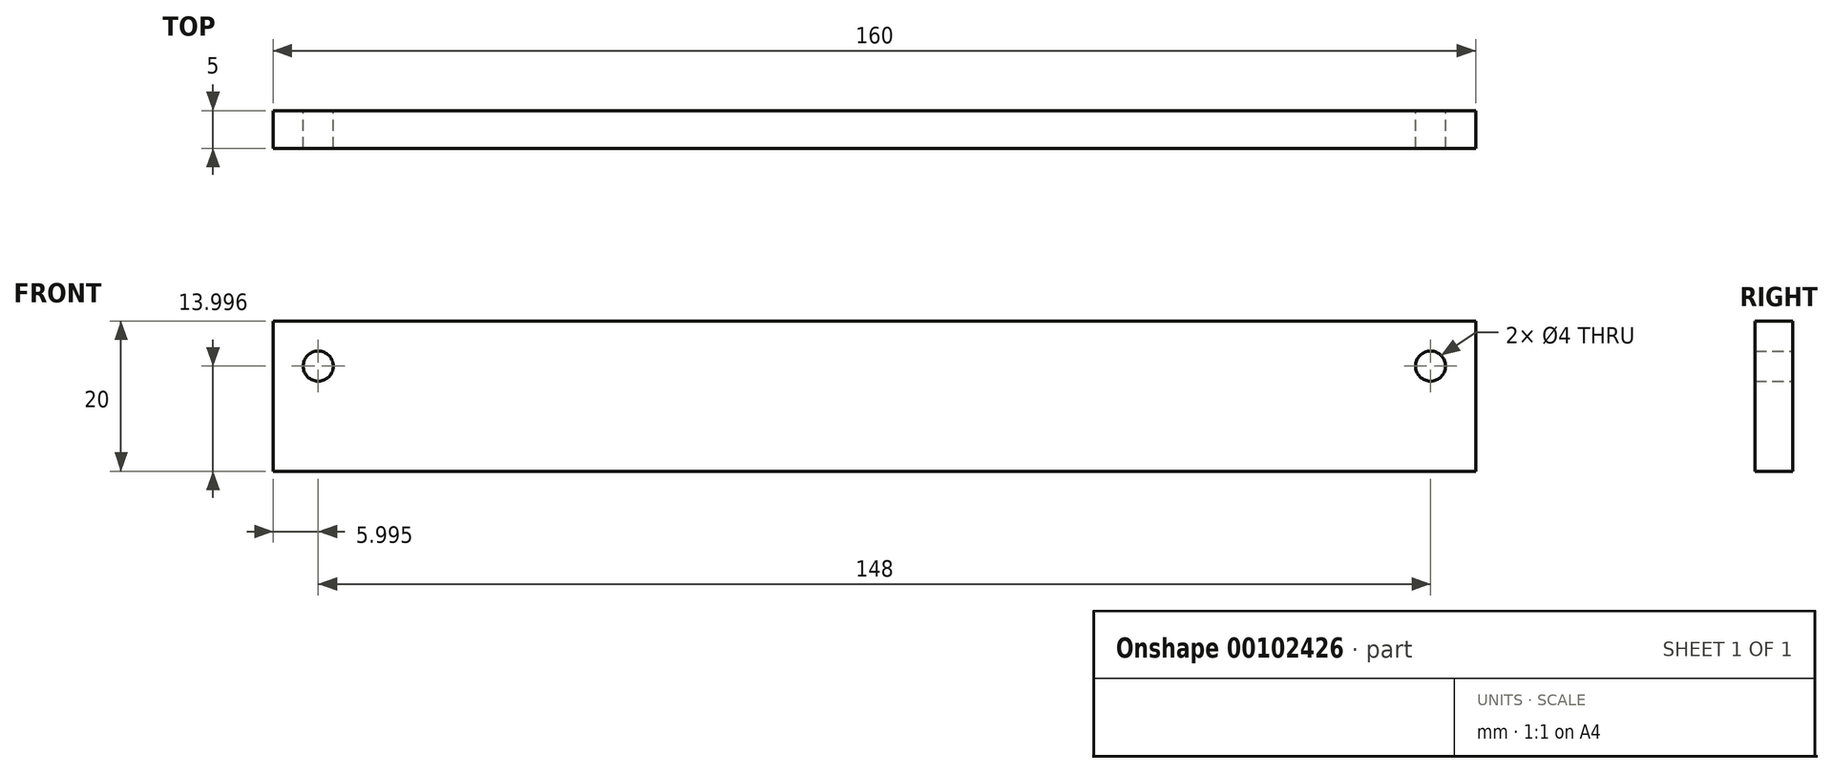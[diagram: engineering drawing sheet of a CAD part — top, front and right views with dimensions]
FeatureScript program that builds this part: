
annotation { "Feature Type Name" : "Feature", "Feature Type Description" : "" }
export const myFeature = defineFeature(function(context is Context, id is Id, definition is map)
    precondition{}
    {
        {
            var Q0;
            Q0=qCreatedBy(makeId("Front.planeOp"),FACE);
            var sketch = newSketch(context, id + "F0", { "sketchPlane" : qUnion([Q0])});
            skLineSegment(sketch, "E0.bottom", {"start": v(-39.16, 10.86) * mm, "end": v(120.84, 10.86) * mm});
            skLineSegment(sketch, "E0.top", {"start": v(-39.16, -9.14) * mm, "end": v(120.84, -9.14) * mm});
            skLineSegment(sketch, "E0.left", {"start": v(-39.16, 10.86) * mm, "end": v(-39.16, -9.14) * mm});
            skLineSegment(sketch, "E0.right", {"start": v(120.84, 10.86) * mm, "end": v(120.84, -9.14) * mm});
            skCircle(sketch, "E1", {"center": v(-33.16, 4.86) * mm, "radius": 2 * mm});
            skCircle(sketch, "E2", {"center": v(114.84, 4.86) * mm, "radius": 2 * mm});
            skSolve(sketch);
        }
        {
            var Q0;
            Q0=makeQuery(id+"F0.imprint","IMPRINT",FACE,{"disambiguationData":[TD([[makeQuery(id+"F0.imprint","IMPRINT",EDGE,{"derivedFrom":sQuery(id+"F0.wireOp",EDGE,"E0.bottom")}),-1.0]])]});
            extrude(context, id + "F1", {"entities" : qUnion([Q0]), "depth" : 5 * mm});
        }
    });
